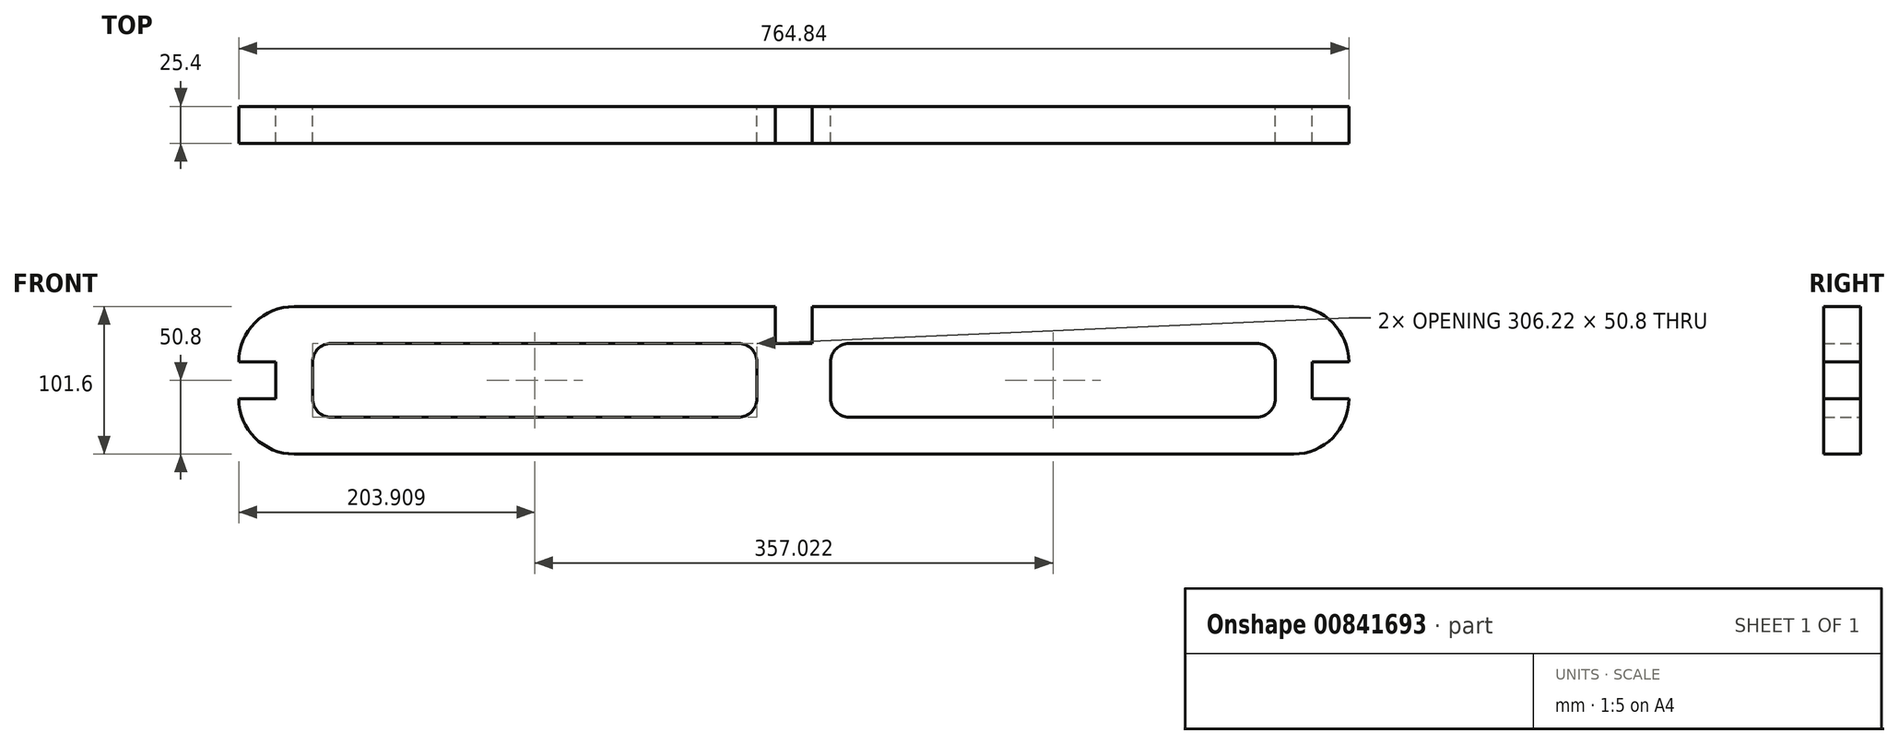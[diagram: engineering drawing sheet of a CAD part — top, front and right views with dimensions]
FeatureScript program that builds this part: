
annotation { "Feature Type Name" : "Feature", "Feature Type Description" : "" }
export const myFeature = defineFeature(function(context is Context, id is Id, definition is map)
    precondition{}
    {
        {
            var Q0;
            Q0=qCreatedBy(makeId("Front.planeOp"),FACE);
            var sketch = newSketch(context, id + "F0", { "sketchPlane" : qUnion([Q0])});
            skLineSegment(sketch, "E0", {"start": v(0, 0) * mm, "end": v(-357.02, 0) * mm, "construction": true});
            skLineSegment(sketch, "E1", {"start": v(0, 0) * mm, "end": v(0, 50.8) * mm, "construction": true});
            skLineSegment(sketch, "E2", {"start": v(-357.02, 12.7) * mm, "end": v(-357.02, -12.7) * mm});
            skLineSegment(sketch, "E3", {"start": v(-357.02, 12.7) * mm, "end": v(-382.42, 12.7) * mm});
            skLineSegment(sketch, "E4", {"start": v(-357.02, -12.7) * mm, "end": v(-382.42, -12.7) * mm});
            skLineSegment(sketch, "E5", {"start": v(-382.42, 12.7) * mm, "end": v(-382.42, -12.7) * mm, "construction": true});
            skLineSegment(sketch, "E6", {"start": v(0, 50.8) * mm, "end": v(-344.32, 50.8) * mm});
            skLineSegment(sketch, "E7", {"start": v(-344.32, 50.8) * mm, "end": v(-344.32, -50.8) * mm, "construction": true});
            skLineSegment(sketch, "E8", {"start": v(-344.32, -50.8) * mm, "end": v(0, -50.8) * mm});
            skLineSegment(sketch, "E9", {"start": v(0, -50.8) * mm, "end": v(0, 0) * mm, "construction": true});
            skArc(sketch, "E10", {"start": v(-344.32, 50.8) * mm, "mid": v(-371.26, 39.64) * mm, "end": v(-382.42, 12.7) * mm});
            skArc(sketch, "E11", {"start": v(-382.42, -12.7) * mm, "mid": v(-371.26, -39.64) * mm, "end": v(-344.32, -50.8) * mm});
            skLineSegment(sketch, "E12.bottom", {"start": v(-318.92, -25.4) * mm, "end": v(-38.1, -25.4) * mm});
            skLineSegment(sketch, "E12.top", {"start": v(-318.92, 25.4) * mm, "end": v(-38.1, 25.4) * mm});
            skLineSegment(sketch, "E12.left", {"start": v(-331.62, -12.7) * mm, "end": v(-331.62, 12.7) * mm});
            skLineSegment(sketch, "E12.right", {"start": v(-25.4, -12.7) * mm, "end": v(-25.4, 12.7) * mm});
            skPoint(sketch, "E13.visualSharp", {"position": v(-331.62, 25.4) * mm});
            skArc(sketch, "E13.filletArc", {"start": v(-318.92, 25.4) * mm, "mid": v(-327.9, 21.68) * mm, "end": v(-331.62, 12.7) * mm});
            skPoint(sketch, "E14.visualSharp", {"position": v(-331.62, -25.4) * mm});
            skArc(sketch, "E14.filletArc", {"start": v(-331.62, -12.7) * mm, "mid": v(-327.9, -21.68) * mm, "end": v(-318.92, -25.4) * mm});
            skPoint(sketch, "E15.visualSharp", {"position": v(-25.4, 25.4) * mm});
            skArc(sketch, "E15.filletArc", {"start": v(-25.4, 12.7) * mm, "mid": v(-29.12, 21.68) * mm, "end": v(-38.1, 25.4) * mm});
            skPoint(sketch, "E16.visualSharp", {"position": v(-25.4, -25.4) * mm});
            skArc(sketch, "E16.filletArc", {"start": v(-38.1, -25.4) * mm, "mid": v(-29.12, -21.68) * mm, "end": v(-25.4, -12.7) * mm});
            skLineSegment(sketch, "E17.MirrorCS", {"start": v(0, 50.8) * mm, "end": v(344.32, 50.8) * mm});
            skArc(sketch, "E18.MirrorCS", {"start": v(344.32, 50.8) * mm, "mid": v(371.26, 39.64) * mm, "end": v(382.42, 12.7) * mm});
            skLineSegment(sketch, "E19.MirrorCS", {"start": v(357.02, 12.7) * mm, "end": v(382.42, 12.7) * mm});
            skLineSegment(sketch, "E20.MirrorCS", {"start": v(357.02, 12.7) * mm, "end": v(357.02, -12.7) * mm});
            skLineSegment(sketch, "E21.MirrorCS", {"start": v(357.02, -12.7) * mm, "end": v(382.42, -12.7) * mm});
            skArc(sketch, "E22.MirrorCS", {"start": v(382.42, -12.7) * mm, "mid": v(371.26, -39.64) * mm, "end": v(344.32, -50.8) * mm});
            skLineSegment(sketch, "E23.MirrorCS", {"start": v(344.32, -50.8) * mm, "end": v(0, -50.8) * mm});
            skLineSegment(sketch, "E24.MirrorCS", {"start": v(318.92, -25.4) * mm, "end": v(38.1, -25.4) * mm});
            skArc(sketch, "E25.MirrorCS", {"start": v(331.62, -12.7) * mm, "mid": v(327.9, -21.68) * mm, "end": v(318.92, -25.4) * mm});
            skLineSegment(sketch, "E26.MirrorCS", {"start": v(331.62, -12.7) * mm, "end": v(331.62, 12.7) * mm});
            skArc(sketch, "E27.MirrorCS", {"start": v(318.92, 25.4) * mm, "mid": v(327.9, 21.68) * mm, "end": v(331.62, 12.7) * mm});
            skLineSegment(sketch, "E28.MirrorCS", {"start": v(318.92, 25.4) * mm, "end": v(38.1, 25.4) * mm});
            skArc(sketch, "E29.MirrorCS", {"start": v(25.4, 12.7) * mm, "mid": v(29.12, 21.68) * mm, "end": v(38.1, 25.4) * mm});
            skLineSegment(sketch, "E30.MirrorCS", {"start": v(25.4, -12.7) * mm, "end": v(25.4, 12.7) * mm});
            skArc(sketch, "E31.MirrorCS", {"start": v(38.1, -25.4) * mm, "mid": v(29.12, -21.68) * mm, "end": v(25.4, -12.7) * mm});
            skSolve(sketch);
        }
        {
            var Q0;
            Q0 = qSketchRegion(id + "F0", true);
            extrude(context, id + "F1", {"entities" : qUnion([Q0]), "depth" : 25.4 * mm, "offsetDistance" : 25.4 * mm});
        }
        {
            var Q0;
            Q0=makeQuery(id+"F1.opExtrude","CAP_FACE",FACE,{"disambiguationData":[OSD([sQuery(id+"F0.wireOp",EDGE,"E2"),sQuery(id+"F0.wireOp",EDGE,"E3"),sQuery(id+"F0.wireOp",EDGE,"E4"),sQuery(id+"F0.wireOp",EDGE,"E6"),sQuery(id+"F0.wireOp",EDGE,"E8"),sQuery(id+"F0.wireOp",EDGE,"E10"),sQuery(id+"F0.wireOp",EDGE,"E11"),sQuery(id+"F0.wireOp",EDGE,"E12.bottom"),sQuery(id+"F0.wireOp",EDGE,"E12.top"),sQuery(id+"F0.wireOp",EDGE,"E12.left"),sQuery(id+"F0.wireOp",EDGE,"E12.right"),sQuery(id+"F0.wireOp",EDGE,"E13.filletArc"),sQuery(id+"F0.wireOp",EDGE,"E14.filletArc"),sQuery(id+"F0.wireOp",EDGE,"E15.filletArc"),sQuery(id+"F0.wireOp",EDGE,"E16.filletArc"),sQuery(id+"F0.wireOp",EDGE,"E17.MirrorCS"),sQuery(id+"F0.wireOp",EDGE,"E18.MirrorCS"),sQuery(id+"F0.wireOp",EDGE,"E19.MirrorCS"),sQuery(id+"F0.wireOp",EDGE,"E20.MirrorCS"),sQuery(id+"F0.wireOp",EDGE,"E21.MirrorCS"),sQuery(id+"F0.wireOp",EDGE,"E22.MirrorCS"),sQuery(id+"F0.wireOp",EDGE,"E23.MirrorCS"),sQuery(id+"F0.wireOp",EDGE,"E24.MirrorCS"),sQuery(id+"F0.wireOp",EDGE,"E25.MirrorCS"),sQuery(id+"F0.wireOp",EDGE,"E26.MirrorCS"),sQuery(id+"F0.wireOp",EDGE,"E27.MirrorCS"),sQuery(id+"F0.wireOp",EDGE,"E28.MirrorCS"),sQuery(id+"F0.wireOp",EDGE,"E29.MirrorCS"),sQuery(id+"F0.wireOp",EDGE,"E30.MirrorCS"),sQuery(id+"F0.wireOp",EDGE,"E31.MirrorCS")])],"isStart":false});
            var sketch = newSketch(context, id + "F2", { "sketchPlane" : qUnion([Q0])});
            skLineSegment(sketch, "E32.bottom", {"start": v(-12.7, 50.8) * mm, "end": v(12.7, 50.8) * mm});
            skLineSegment(sketch, "E32.top", {"start": v(-12.7, 25.4) * mm, "end": v(12.7, 25.4) * mm});
            skLineSegment(sketch, "E32.left", {"start": v(-12.7, 50.8) * mm, "end": v(-12.7, 25.4) * mm});
            skLineSegment(sketch, "E32.right", {"start": v(12.7, 50.8) * mm, "end": v(12.7, 25.4) * mm});
            skLineSegment(sketch, "E33.bottom", {"start": v(-12.7, -50.8) * mm, "end": v(12.7, -50.8) * mm});
            skLineSegment(sketch, "E33.top", {"start": v(-12.7, -25.4) * mm, "end": v(12.7, -25.4) * mm});
            skLineSegment(sketch, "E33.left", {"start": v(-12.7, -50.8) * mm, "end": v(-12.7, -25.4) * mm});
            skLineSegment(sketch, "E33.right", {"start": v(12.7, -50.8) * mm, "end": v(12.7, -25.4) * mm});
            skLineSegment(sketch, "E34", {"start": v(0, 0) * mm, "end": v(0, 25.4) * mm, "construction": true});
            skLineSegment(sketch, "E35", {"start": v(0, 0) * mm, "end": v(0, -25.4) * mm, "construction": true});
            skSolve(sketch);
        }
        {
            var Q0;
            Q0=makeQuery(id+"F2.imprint","IMPRINT",FACE,{"disambiguationData":[TD([[makeQuery(id+"F2.imprint","IMPRINT",EDGE,{"derivedFrom":sQuery(id+"F2.wireOp",EDGE,"E32.bottom")}),-1.0]])]});
            var Q1;
            Q1=makeQuery(id+"F2.imprint","IMPRINT",FACE,{"disambiguationData":[TD([[makeQuery(id+"F2.imprint","IMPRINT",EDGE,{"derivedFrom":sQuery(id+"F2.wireOp",EDGE,"E33.bottom")}),-1.0]])]});
            extrude(context, id + "F3", {"entities" : qUnion([Q0, Q1]), "operationType" : NewBodyOperationType.REMOVE, "oppositeDirection" : true, "depth" : 25.4 * mm, "offsetDistance" : 25.4 * mm});
        }
    });
